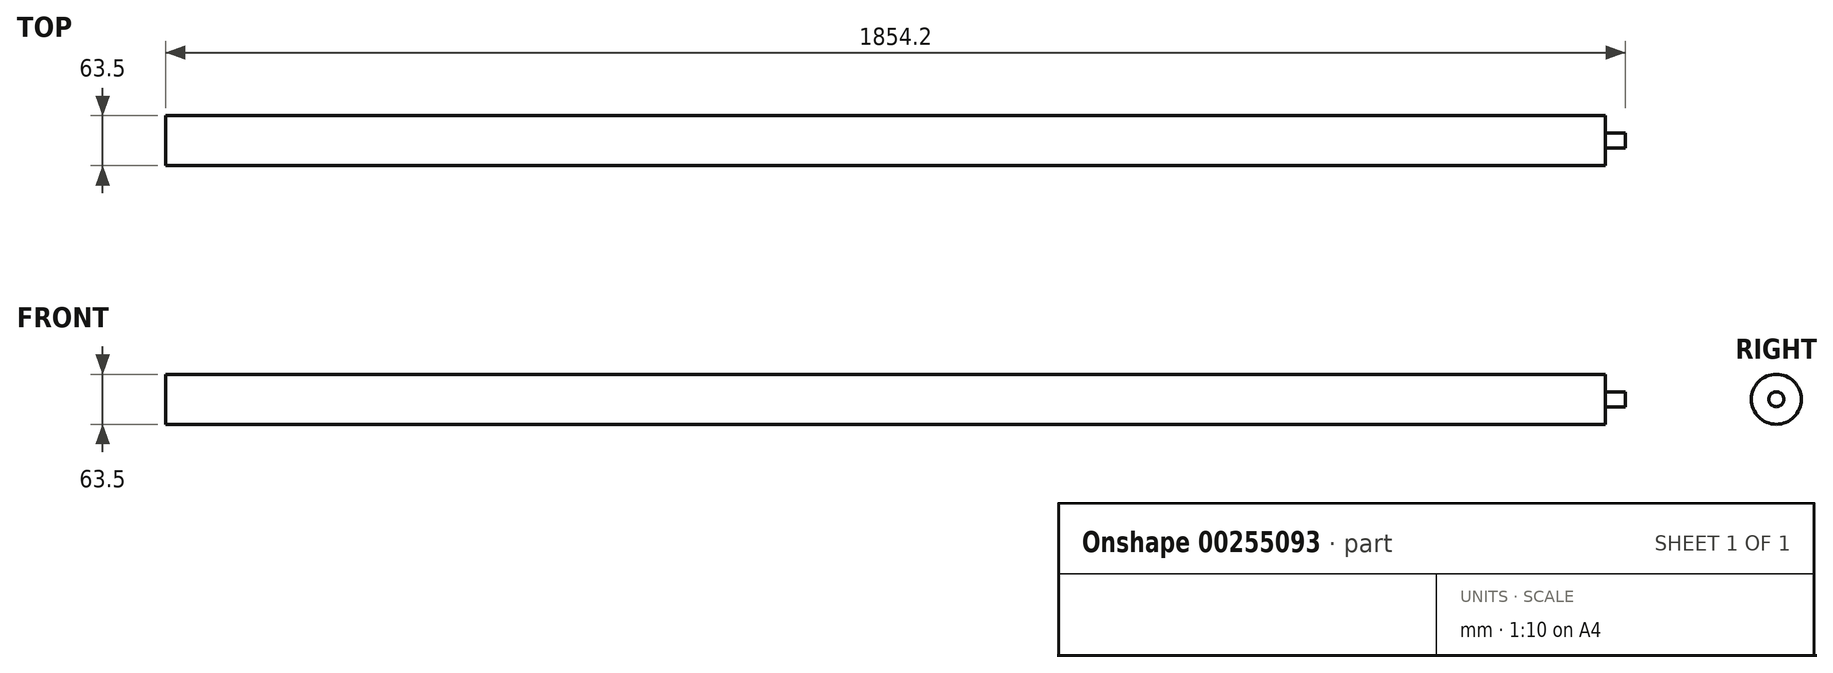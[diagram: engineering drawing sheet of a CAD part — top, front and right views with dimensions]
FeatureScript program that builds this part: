
annotation { "Feature Type Name" : "Feature", "Feature Type Description" : "" }
export const myFeature = defineFeature(function(context is Context, id is Id, definition is map)
    precondition{}
    {
        {
            var Q0;
            Q0=qCreatedBy(makeId("Right.planeOp"),FACE);
            var sketch = newSketch(context, id + "F0", { "sketchPlane" : qUnion([Q0])});
            skCircle(sketch, "E0", {"center": v(0, 0) * mm, "radius": 9.52 * mm});
            skSolve(sketch);
        }
        {
            var Q0;
            Q0 = qSketchRegion(id + "F0", true);
            extrude(context, id + "F1", {"entities" : qUnion([Q0]), "depth" : 25.4 * mm});
        }
        {
            var Q0;
            Q0=makeQuery(id+"F1.opExtrude","CAP_FACE",FACE,{"disambiguationData":[OSD([sQuery(id+"F0.wireOp",EDGE,"E0")])],"isStart":true});
            var sketch = newSketch(context, id + "F2", { "sketchPlane" : qUnion([Q0])});
            skCircle(sketch, "E1", {"center": v(0, 0) * mm, "radius": 31.75 * mm});
            skSolve(sketch);
        }
        {
            var Q0;
            Q0 = qSketchRegion(id + "F2", true);
            extrude(context, id + "F3", {"entities" : qUnion([Q0]), "operationType" : NewBodyOperationType.ADD, "depth" : 1828.8 * mm});
        }
    });
